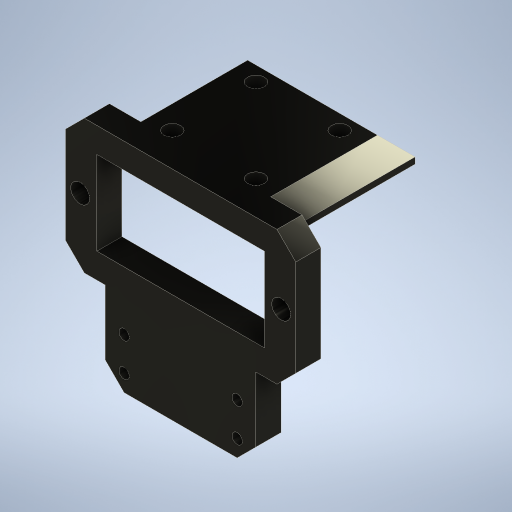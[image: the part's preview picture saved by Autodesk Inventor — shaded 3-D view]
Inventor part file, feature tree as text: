
AUTODESK INVENTOR PART (.ipt)
format: ipt  version: 2024.3 (Build 283343000, 343)  size: 322,560 bytes
history: native  units: mm
features: extrude x4, sketch x4, chamfer x3
ambient origin geometry x8: Origin, YZ Plane, XZ Plane, XY Plane, X Axis, Y Axis, Z Axis, Center Point
bodies: Solid1 (feature_tree)
feature tree (11):
  extrude  "Extrusion1"  Depth=20.0mm
  chamfer  "Chamfer1"  Distance=24.0mm
  extrude  "Extrusion3"  Depth=6.0mm TaperAngle=0.0deg
  chamfer  "Chamfer2"  Distance=2.0mm Angle=45.0deg
  extrude  "Extrusion4"  Depth=10.0mm
  chamfer  "Chamfer3"  Distance=5.0mm
  extrude  "Extrusion2"  Depth=20.0mm
  sketch  "Sketch1"  dims[d0=40.0mm d1=20.0mm]
  sketch  "Sketch2"  dims[d2=32.0mm]
  sketch  "Sketch3"  dims[d3=55.0mm]
  sketch  "Sketch6"  dims[d4=4.5mm d5=24.0mm d6=6.0mm d7=0.0mm d8=4.5mm d9=2.0mm d10=45.0deg d11=10.0mm d13=5.0mm d14=0.0mm d17=18.0mm d18=20.0mm d19=2.5mm d20=2.5mm d21=8.0mm d22=16.0mm d23=6.0mm d24=0.0mm d26=13.5mm d27=4.5mm d28=2.0mm d29=45.0deg d30=40.0mm d31=30.0mm d32=0.0mm d33=4.5mm d34=2.0mm d35=45.0deg d36=5.0mm d37=4.0mm d38=20.0mm d40=20.0mm d41=20.0mm d43=20.0mm d25=0.5mm]
